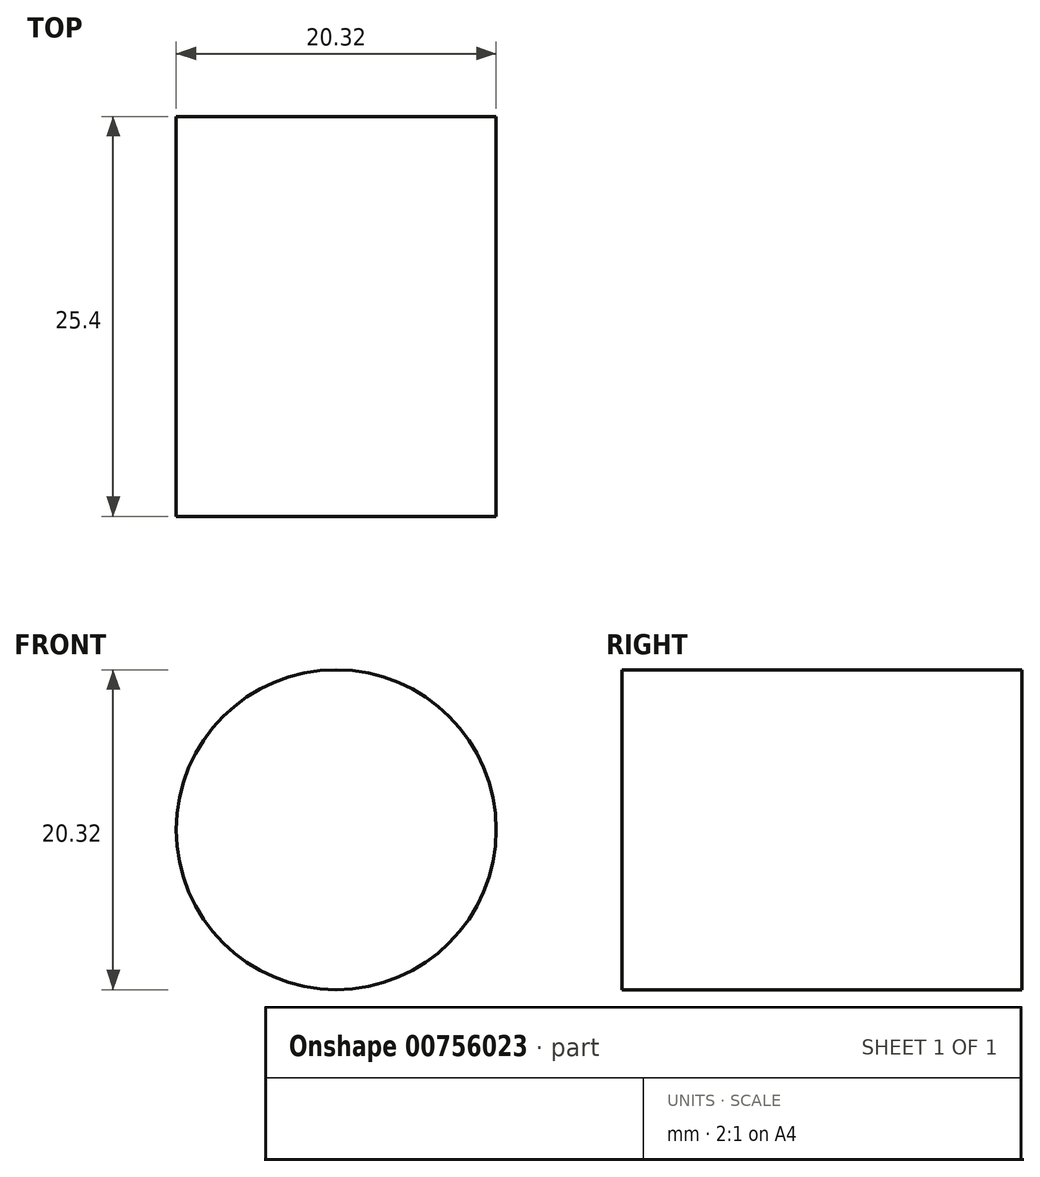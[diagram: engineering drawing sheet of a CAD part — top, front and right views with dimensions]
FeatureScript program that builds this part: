
annotation { "Feature Type Name" : "Feature", "Feature Type Description" : "" }
export const myFeature = defineFeature(function(context is Context, id is Id, definition is map)
    precondition{}
    {
        {
            var Q0;
            Q0=qCreatedBy(makeId("Front.planeOp"),FACE);
            var sketch = newSketch(context, id + "F0", { "sketchPlane" : qUnion([Q0])});
            skCircle(sketch, "E0", {"center": v(0, 0) * mm, "radius": 10.16 * mm});
            skSolve(sketch);
        }
        {
            var Q0;
            Q0=makeQuery(id+"F0.imprint","IMPRINT",FACE,{"disambiguationData":[TD([[makeQuery(id+"F0.imprint","IMPRINT",EDGE,{"derivedFrom":sQuery(id+"F0.wireOp",EDGE,"E0")}),1.0]])]});
            extrude(context, id + "F1", {"entities" : qUnion([Q0]), "depth" : 25.4 * mm, "offsetDistance" : 25.4 * mm});
        }
    });
